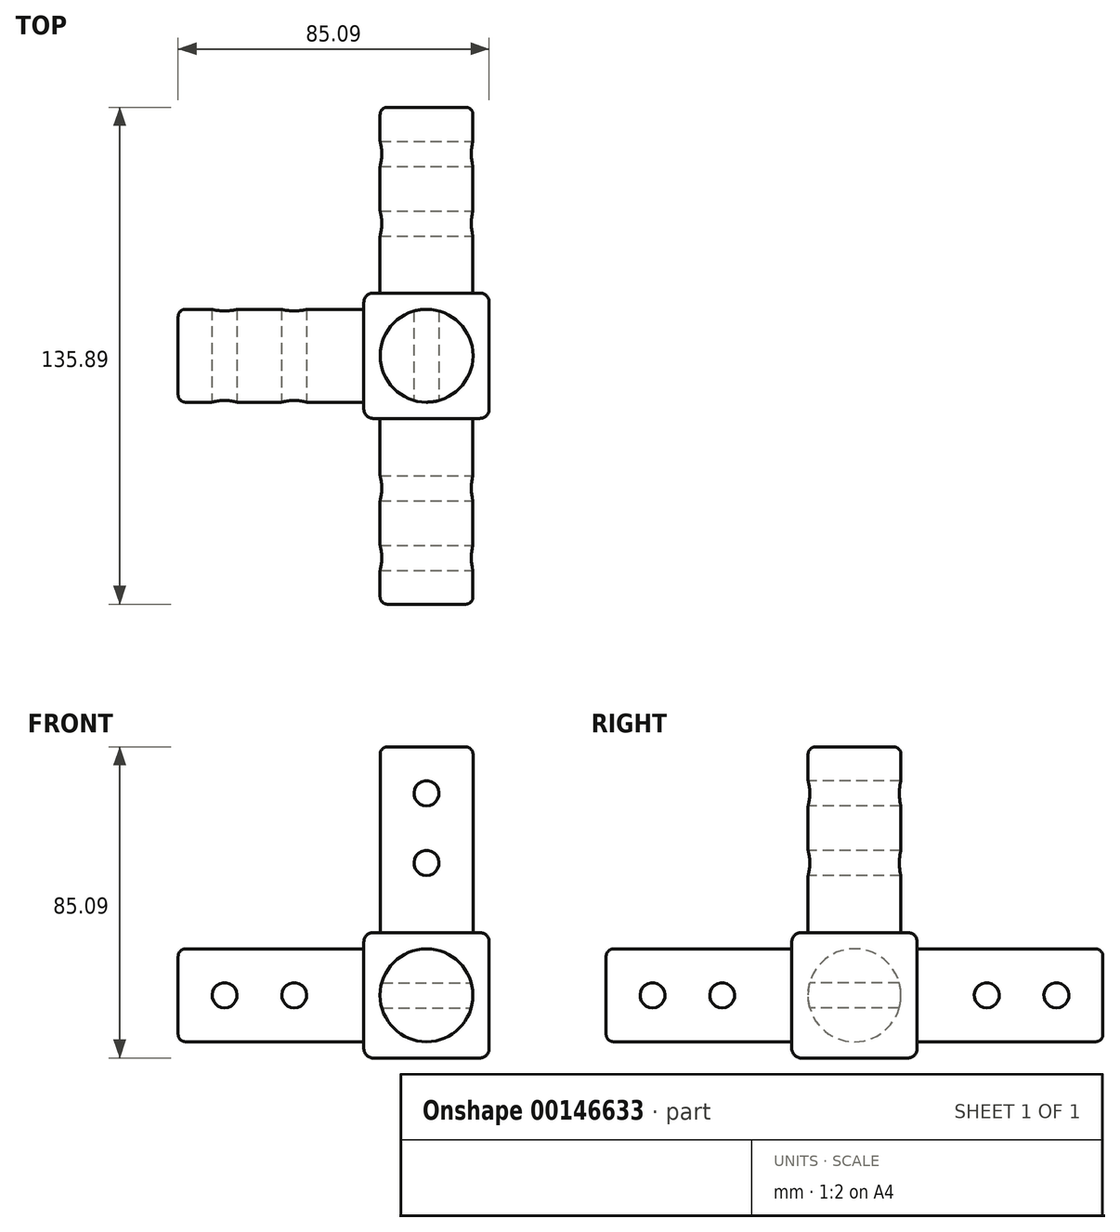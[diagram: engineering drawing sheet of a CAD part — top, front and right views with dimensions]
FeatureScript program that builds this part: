
annotation { "Feature Type Name" : "Feature", "Feature Type Description" : "" }
export const myFeature = defineFeature(function(context is Context, id is Id, definition is map)
    precondition{}
    {
        {
            var Q0;
            Q0=qCreatedBy(makeId("Top.planeOp"),FACE);
            var sketch = newSketch(context, id + "F0", { "sketchPlane" : qUnion([Q0])});
            skLineSegment(sketch, "E0.bottom", {"start": v(-13.47, 23.7) * mm, "end": v(20.82, 23.7) * mm});
            skLineSegment(sketch, "E0.top", {"start": v(-13.47, -10.58) * mm, "end": v(20.82, -10.58) * mm});
            skLineSegment(sketch, "E0.left", {"start": v(-13.47, 23.7) * mm, "end": v(-13.47, -10.58) * mm});
            skLineSegment(sketch, "E0.right", {"start": v(20.82, 23.7) * mm, "end": v(20.82, -10.58) * mm});
            skSolve(sketch);
        }
        {
            var Q0;
            Q0=qSketchRegion(id+"F0",true);
            extrude(context, id + "F1", {"entities" : qUnion([Q0]), "depth" : 34.3 * mm});
        }
        {
            var Q0;
            Q0=makeQuery(id+"F1.opExtrude","CAP_FACE",FACE,{"disambiguationData":[OSD([sQuery(id+"F0.wireOp",EDGE,"E0.bottom"),sQuery(id+"F0.wireOp",EDGE,"E0.top"),sQuery(id+"F0.wireOp",EDGE,"E0.left"),sQuery(id+"F0.wireOp",EDGE,"E0.right")])],"isStart":false});
            var sketch = newSketch(context, id + "F2", { "sketchPlane" : qUnion([Q0])});
            skCircle(sketch, "E1", {"center": v(3.68, 6.56) * mm, "radius": 12.7 * mm});
            skLineSegment(sketch, "E2", {"start": v(3.67, 23.7) * mm, "end": v(3.67, -12.79) * mm, "construction": true});
            skLineSegment(sketch, "E3", {"start": v(20.82, 6.56) * mm, "end": v(-13.47, 6.56) * mm, "construction": true});
            skSolve(sketch);
        }
        {
            var Q0;
            Q0=qSketchRegion(id+"F2",true);
            extrude(context, id + "F3", {"entities" : qUnion([Q0]), "operationType" : NewBodyOperationType.ADD, "depth" : 50.8 * mm});
        }
        {
            var Q0;
            Q0=makeQuery(id+"F1.opExtrude","SWEPT_FACE",FACE,{"disambiguationData":[OSD([sQuery(id+"F0.wireOp",EDGE,"E0.left")])]});
            var sketch = newSketch(context, id + "F4", { "sketchPlane" : qUnion([Q0])});
            skLineSegment(sketch, "E4", {"start": v(-23.7, 17.15) * mm, "end": v(13.45, 17.15) * mm, "construction": true});
            skLineSegment(sketch, "E5", {"start": v(-6.56, 0) * mm, "end": v(-6.56, 34.3) * mm, "construction": true});
            skCircle(sketch, "E6", {"center": v(-6.56, 17.15) * mm, "radius": 12.7 * mm});
            skSolve(sketch);
        }
        {
            var Q0;
            Q0=qSketchRegion(id+"F4",true);
            extrude(context, id + "F5", {"entities" : qUnion([Q0]), "operationType" : NewBodyOperationType.ADD, "depth" : 50.8 * mm});
        }
        {
            var Q0;
            Q0=makeQuery(id+"F1.opExtrude","SWEPT_FACE",FACE,{"disambiguationData":[OSD([sQuery(id+"F0.wireOp",EDGE,"E0.top")])]});
            var sketch = newSketch(context, id + "F6", { "sketchPlane" : qUnion([Q0])});
            skLineSegment(sketch, "E7", {"start": v(-13.47, 17.15) * mm, "end": v(24.43, 17.15) * mm, "construction": true});
            skLineSegment(sketch, "E8", {"start": v(3.67, 0) * mm, "end": v(3.67, 34.3) * mm, "construction": true});
            skCircle(sketch, "E9", {"center": v(3.67, 17.15) * mm, "radius": 12.7 * mm});
            skSolve(sketch);
        }
        {
            var Q0;
            Q0=qSketchRegion(id+"F6",true);
            extrude(context, id + "F7", {"entities" : qUnion([Q0]), "operationType" : NewBodyOperationType.ADD, "depth" : 50.8 * mm});
        }
        {
            var Q0;
            Q0=qCreatedBy(makeId("Front.planeOp"),FACE);
            var sketch = newSketch(context, id + "F8", { "sketchPlane" : qUnion([Q0])});
            skCircle(sketch, "E10", {"center": v(3.67, 53.34) * mm, "radius": 3.43 * mm});
            skCircle(sketch, "E11", {"center": v(3.67, 72.4) * mm, "radius": 3.43 * mm});
            skSolve(sketch);
        }
        {
            var Q0;
            Q0=qSketchRegion(id+"F8",true);
            extrude(context, id + "F9", {"entities" : qUnion([Q0]), "operationType" : NewBodyOperationType.REMOVE, "endBound" : BoundingType.SYMMETRIC, "oppositeDirection" : true, "depth" : 50.8 * mm});
        }
        {
            var Q0;
            Q0=qCreatedBy(makeId("Right.planeOp"),FACE);
            var sketch = newSketch(context, id + "F10", { "sketchPlane" : qUnion([Q0])});
            skCircle(sketch, "E12", {"center": v(-29.63, 17.15) * mm, "radius": 3.43 * mm});
            skCircle(sketch, "E13", {"center": v(-48.68, 17.15) * mm, "radius": 3.43 * mm});
            skSolve(sketch);
        }
        {
            var Q0;
            Q0=qSketchRegion(id+"F10",true);
            extrude(context, id + "F11", {"entities" : qUnion([Q0]), "operationType" : NewBodyOperationType.REMOVE, "endBound" : BoundingType.SYMMETRIC, "oppositeDirection" : true, "depth" : 50.8 * mm});
        }
        {
            var Q0;
            Q0=qCreatedBy(makeId("Front.planeOp"),FACE);
            var sketch = newSketch(context, id + "F12", { "sketchPlane" : qUnion([Q0])});
            skCircle(sketch, "E14", {"center": v(-51.57, 17.15) * mm, "radius": 3.43 * mm});
            skCircle(sketch, "E15", {"center": v(-32.52, 17.15) * mm, "radius": 3.43 * mm});
            skSolve(sketch);
        }
        {
            var Q0;
            Q0=qSketchRegion(id+"F12",true);
            extrude(context, id + "F13", {"entities" : qUnion([Q0]), "operationType" : NewBodyOperationType.REMOVE, "endBound" : BoundingType.SYMMETRIC, "oppositeDirection" : true, "depth" : 50.8 * mm});
        }
        {
            var Q0;
            Q0=makeQuery(id+"F1.opExtrude","SWEPT_EDGE",EDGE,{"disambiguationData":[OSD([sQuery(id+"F0.wireOp",EDGE,"E0.bottom"),sQuery(id+"F0.wireOp",EDGE,"E0.right")])]});
            var Q1;
            Q1=makeQuery(id+"F1.opExtrude","CAP_EDGE",EDGE,{"disambiguationData":[OSD([sQuery(id+"F0.wireOp",EDGE,"E0.right")])],"isStart":false});
            var Q2;
            Q2=makeQuery(id+"F1.opExtrude","SWEPT_EDGE",EDGE,{"disambiguationData":[OSD([sQuery(id+"F0.wireOp",EDGE,"E0.top"),sQuery(id+"F0.wireOp",EDGE,"E0.right")])]});
            var Q3;
            Q3=makeQuery(id+"F1.opExtrude","CAP_EDGE",EDGE,{"disambiguationData":[OSD([sQuery(id+"F0.wireOp",EDGE,"E0.right")])],"isStart":true});
            var Q4;
            Q4=makeQuery(id+"F1.opExtrude","CAP_EDGE",EDGE,{"disambiguationData":[OSD([sQuery(id+"F0.wireOp",EDGE,"E0.bottom")])],"isStart":true});
            var Q5;
            Q5=makeQuery(id+"F1.opExtrude","CAP_EDGE",EDGE,{"disambiguationData":[OSD([sQuery(id+"F0.wireOp",EDGE,"E0.bottom")])],"isStart":false});
            var Q6;
            Q6=makeQuery(id+"F1.opExtrude","SWEPT_EDGE",EDGE,{"disambiguationData":[OSD([sQuery(id+"F0.wireOp",EDGE,"E0.bottom"),sQuery(id+"F0.wireOp",EDGE,"E0.left")])]});
            var Q7;
            Q7=makeQuery(id+"F1.opExtrude","CAP_EDGE",EDGE,{"disambiguationData":[OSD([sQuery(id+"F0.wireOp",EDGE,"E0.left")])],"isStart":true});
            var Q8;
            Q8=makeQuery(id+"F1.opExtrude","CAP_EDGE",EDGE,{"disambiguationData":[OSD([sQuery(id+"F0.wireOp",EDGE,"E0.top")])],"isStart":true});
            var Q9;
            Q9=makeQuery(id+"F1.opExtrude","CAP_EDGE",EDGE,{"disambiguationData":[OSD([sQuery(id+"F0.wireOp",EDGE,"E0.left")])],"isStart":false});
            var Q10;
            Q10=makeQuery(id+"F1.opExtrude","SWEPT_EDGE",EDGE,{"disambiguationData":[OSD([sQuery(id+"F0.wireOp",EDGE,"E0.top"),sQuery(id+"F0.wireOp",EDGE,"E0.left")])]});
            var Q11;
            Q11=makeQuery(id+"F1.opExtrude","CAP_EDGE",EDGE,{"disambiguationData":[OSD([sQuery(id+"F0.wireOp",EDGE,"E0.top")])],"isStart":false});
            fillet(context, id + "F14", {"entities" : qUnion([Q0, Q1, Q2, Q3, Q4, Q5, Q6, Q7, Q8, Q9, Q10, Q11]), "radius" : 2.54 * mm, "tangentPropagation" : true, "allowEdgeOverflow" : false});
        }
        {
            var Q0;
            Q0=makeQuery(id+"F1.opExtrude","SWEPT_FACE",FACE,{"disambiguationData":[OSD([sQuery(id+"F0.wireOp",EDGE,"E0.bottom")])]});
            var sketch = newSketch(context, id + "F15", { "sketchPlane" : qUnion([Q0])});
            skLineSegment(sketch, "E16", {"start": v(-18.28, 17.15) * mm, "end": v(4.82, 17.15) * mm, "construction": true});
            skPoint(sketch, "E16.endSnap0", {"position": v(-18.28, 17.15) * mm});
            skLineSegment(sketch, "E17", {"start": v(-3.67, 31.75) * mm, "end": v(-3.67, 14.65) * mm, "construction": true});
            skCircle(sketch, "E18", {"center": v(-3.67, 17.15) * mm, "radius": 12.7 * mm});
            skSolve(sketch);
        }
        {
            var Q0;
            Q0 = qSketchRegion(id + "F15", true);
            extrude(context, id + "F16", {"entities" : qUnion([Q0]), "operationType" : NewBodyOperationType.ADD, "depth" : 50.8 * mm});
        }
        {
            var Q0;
            Q0=qCreatedBy(makeId("Right.planeOp"),FACE);
            var sketch = newSketch(context, id + "F17", { "sketchPlane" : qUnion([Q0])});
            skCircle(sketch, "E19", {"center": v(42.76, 17.15) * mm, "radius": 3.43 * mm});
            skCircle(sketch, "E20", {"center": v(61.8, 17.15) * mm, "radius": 3.43 * mm});
            skSolve(sketch);
        }
        {
            var Q0;
            Q0 = qSketchRegion(id + "F17", true);
            extrude(context, id + "F18", {"entities" : qUnion([Q0]), "operationType" : NewBodyOperationType.REMOVE, "endBound" : BoundingType.SYMMETRIC, "oppositeDirection" : true, "depth" : 50.8 * mm});
        }
        {
            var Q0;
            Q0=makeQuery(id+"F3.opExtrude","CAP_EDGE",EDGE,{"disambiguationData":[OSD([sQuery(id+"F2.wireOp",EDGE,"E1")])],"isStart":false});
            var Q1;
            Q1=makeQuery(id+"F7.opExtrude","CAP_EDGE",EDGE,{"disambiguationData":[OSD([sQuery(id+"F6.wireOp",EDGE,"E9")])],"isStart":false});
            var Q2;
            Q2=makeQuery(id+"F5.opExtrude","CAP_EDGE",EDGE,{"disambiguationData":[OSD([sQuery(id+"F4.wireOp",EDGE,"E6")])],"isStart":false});
            var Q3;
            Q3=makeQuery(id+"F16.opExtrude","CAP_EDGE",EDGE,{"disambiguationData":[OSD([sQuery(id+"F15.wireOp",EDGE,"E18")])],"isStart":false});
            fillet(context, id + "F19", {"entities" : qUnion([Q0, Q1, Q2, Q3]), "radius" : 2.03 * mm, "tangentPropagation" : true, "allowEdgeOverflow" : false});
        }
    });
